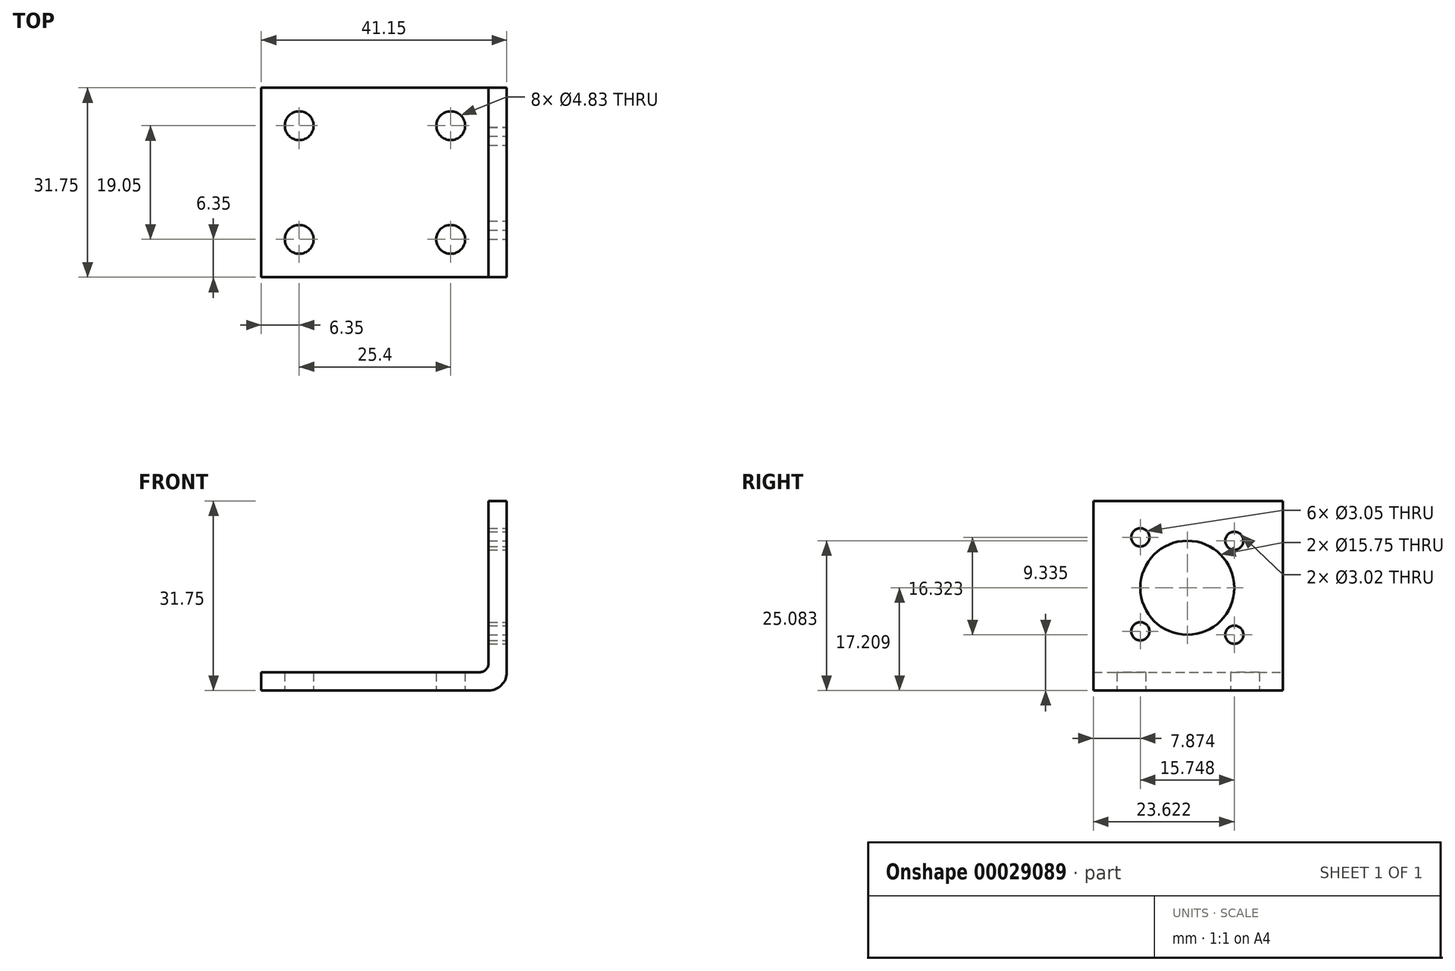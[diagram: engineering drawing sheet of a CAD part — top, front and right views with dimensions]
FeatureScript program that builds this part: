
annotation { "Feature Type Name" : "Feature", "Feature Type Description" : "" }
export const myFeature = defineFeature(function(context is Context, id is Id, definition is map)
    precondition{}
    {
        {
            var Q0;
            Q0=qCreatedBy(makeId("Front.planeOp"),FACE);
            var sketch = newSketch(context, id + "F0", { "sketchPlane" : qUnion([Q0])});
            skLineSegment(sketch, "E0", {"start": v(0, 0) * mm, "end": v(38.1, 0) * mm});
            skLineSegment(sketch, "E1", {"start": v(41.15, 3.05) * mm, "end": v(41.15, 31.75) * mm});
            skLineSegment(sketch, "E2", {"start": v(41.15, 31.75) * mm, "end": v(38.1, 31.75) * mm});
            skLineSegment(sketch, "E3", {"start": v(38.1, 31.75) * mm, "end": v(38.1, 4.57) * mm});
            skLineSegment(sketch, "E4", {"start": v(36.58, 3.05) * mm, "end": v(0, 3.05) * mm});
            skPoint(sketch, "E5.visualSharp", {"position": v(38.1, 3.05) * mm});
            skArc(sketch, "E5.filletArc", {"start": v(36.58, 3.05) * mm, "mid": v(37.65, 3.5) * mm, "end": v(38.1, 4.57) * mm});
            skPoint(sketch, "E6.visualSharp", {"position": v(41.15, 0) * mm});
            skArc(sketch, "E6.filletArc", {"start": v(38.1, 0) * mm, "mid": v(40.26, 0.9) * mm, "end": v(41.15, 3.05) * mm});
            skLineSegment(sketch, "E7", {"start": v(0, 3.05) * mm, "end": v(0, 0) * mm});
            skSolve(sketch);
        }
        {
            var Q0;
            Q0=makeQuery(id+"F0.imprint","IMPRINT",FACE,{"disambiguationData":[TD([[makeQuery(id+"F0.imprint","IMPRINT",EDGE,{"derivedFrom":sQuery(id+"F0.wireOp",EDGE,"E0")}),1.0]])]});
            extrude(context, id + "F1", {"entities" : qUnion([Q0]), "depth" : 31.75 * mm});
        }
        {
            var Q0;
            Q0=makeQuery(id+"F1.opExtrude","SWEPT_FACE",FACE,{"disambiguationData":[OSD([sQuery(id+"F0.wireOp",EDGE,"E1")])]});
            var sketch = newSketch(context, id + "F2", { "sketchPlane" : qUnion([Q0])});
            skCircle(sketch, "E8", {"center": v(-16, 17.2) * mm, "radius": 7.87 * mm});
            skCircle(sketch, "E9", {"center": v(-23.88, 25.66) * mm, "radius": 1.52 * mm});
            skCircle(sketch, "E10", {"center": v(-23.88, 9.91) * mm, "radius": 1.52 * mm});
            skCircle(sketch, "E11", {"center": v(-8.13, 9.34) * mm, "radius": 1.52 * mm});
            skCircle(sketch, "E12", {"center": v(-8.13, 25.08) * mm, "radius": 1.51 * mm});
            skSolve(sketch);
        }
        {
            var Q0;
            Q0=makeQuery(id+"F2.imprint","IMPRINT",FACE,{"disambiguationData":[TD([[makeQuery(id+"F2.imprint","IMPRINT",EDGE,{"derivedFrom":sQuery(id+"F2.wireOp",EDGE,"E9")}),1.0]])]});
            var Q1;
            Q1=makeQuery(id+"F2.imprint","IMPRINT",FACE,{"disambiguationData":[TD([[makeQuery(id+"F2.imprint","IMPRINT",EDGE,{"derivedFrom":sQuery(id+"F2.wireOp",EDGE,"E12")}),1.0]])]});
            var Q2;
            Q2=makeQuery(id+"F2.imprint","IMPRINT",FACE,{"disambiguationData":[TD([[makeQuery(id+"F2.imprint","IMPRINT",EDGE,{"derivedFrom":sQuery(id+"F2.wireOp",EDGE,"E11")}),1.0]])]});
            var Q3;
            Q3=makeQuery(id+"F2.imprint","IMPRINT",FACE,{"disambiguationData":[TD([[makeQuery(id+"F2.imprint","IMPRINT",EDGE,{"derivedFrom":sQuery(id+"F2.wireOp",EDGE,"E10")}),1.0]])]});
            var Q4;
            Q4=makeQuery(id+"F2.imprint","IMPRINT",FACE,{"disambiguationData":[TD([[makeQuery(id+"F2.imprint","IMPRINT",EDGE,{"derivedFrom":sQuery(id+"F2.wireOp",EDGE,"E8")}),1.0]])]});
            extrude(context, id + "F3", {"entities" : qUnion([Q0, Q1, Q2, Q3, Q4]), "operationType" : NewBodyOperationType.REMOVE, "endBound" : BoundingType.THROUGH_ALL, "oppositeDirection" : true, "depth" : 25.4 * mm});
        }
        {
            var Q0;
            Q0=makeQuery(id+"F1.opExtrude","SWEPT_FACE",FACE,{"disambiguationData":[OSD([sQuery(id+"F0.wireOp",EDGE,"E0")])]});
            var sketch = newSketch(context, id + "F4", { "sketchPlane" : qUnion([Q0])});
            skCircle(sketch, "E13", {"center": v(6.35, 25.4) * mm, "radius": 2.41 * mm});
            skCircle(sketch, "E14", {"center": v(31.74, 25.4) * mm, "radius": 2.41 * mm});
            skCircle(sketch, "E15", {"center": v(6.35, 6.35) * mm, "radius": 2.41 * mm});
            skCircle(sketch, "E16", {"center": v(31.75, 6.35) * mm, "radius": 2.41 * mm});
            skSolve(sketch);
        }
        {
            var Q0;
            Q0=makeQuery(id+"F4.imprint","IMPRINT",FACE,{"disambiguationData":[TD([[makeQuery(id+"F4.imprint","IMPRINT",EDGE,{"derivedFrom":sQuery(id+"F4.wireOp",EDGE,"E13")}),1.0]])]});
            var Q1;
            Q1=makeQuery(id+"F4.imprint","IMPRINT",FACE,{"disambiguationData":[TD([[makeQuery(id+"F4.imprint","IMPRINT",EDGE,{"derivedFrom":sQuery(id+"F4.wireOp",EDGE,"E14")}),1.0]])]});
            var Q2;
            Q2=makeQuery(id+"F4.imprint","IMPRINT",FACE,{"disambiguationData":[TD([[makeQuery(id+"F4.imprint","IMPRINT",EDGE,{"derivedFrom":sQuery(id+"F4.wireOp",EDGE,"E16")}),1.0]])]});
            var Q3;
            Q3=makeQuery(id+"F4.imprint","IMPRINT",FACE,{"disambiguationData":[TD([[makeQuery(id+"F4.imprint","IMPRINT",EDGE,{"derivedFrom":sQuery(id+"F4.wireOp",EDGE,"E15")}),1.0]])]});
            extrude(context, id + "F5", {"entities" : qUnion([Q0, Q1, Q2, Q3]), "operationType" : NewBodyOperationType.REMOVE, "endBound" : BoundingType.THROUGH_ALL, "oppositeDirection" : true, "depth" : 25.4 * mm});
        }
    });
